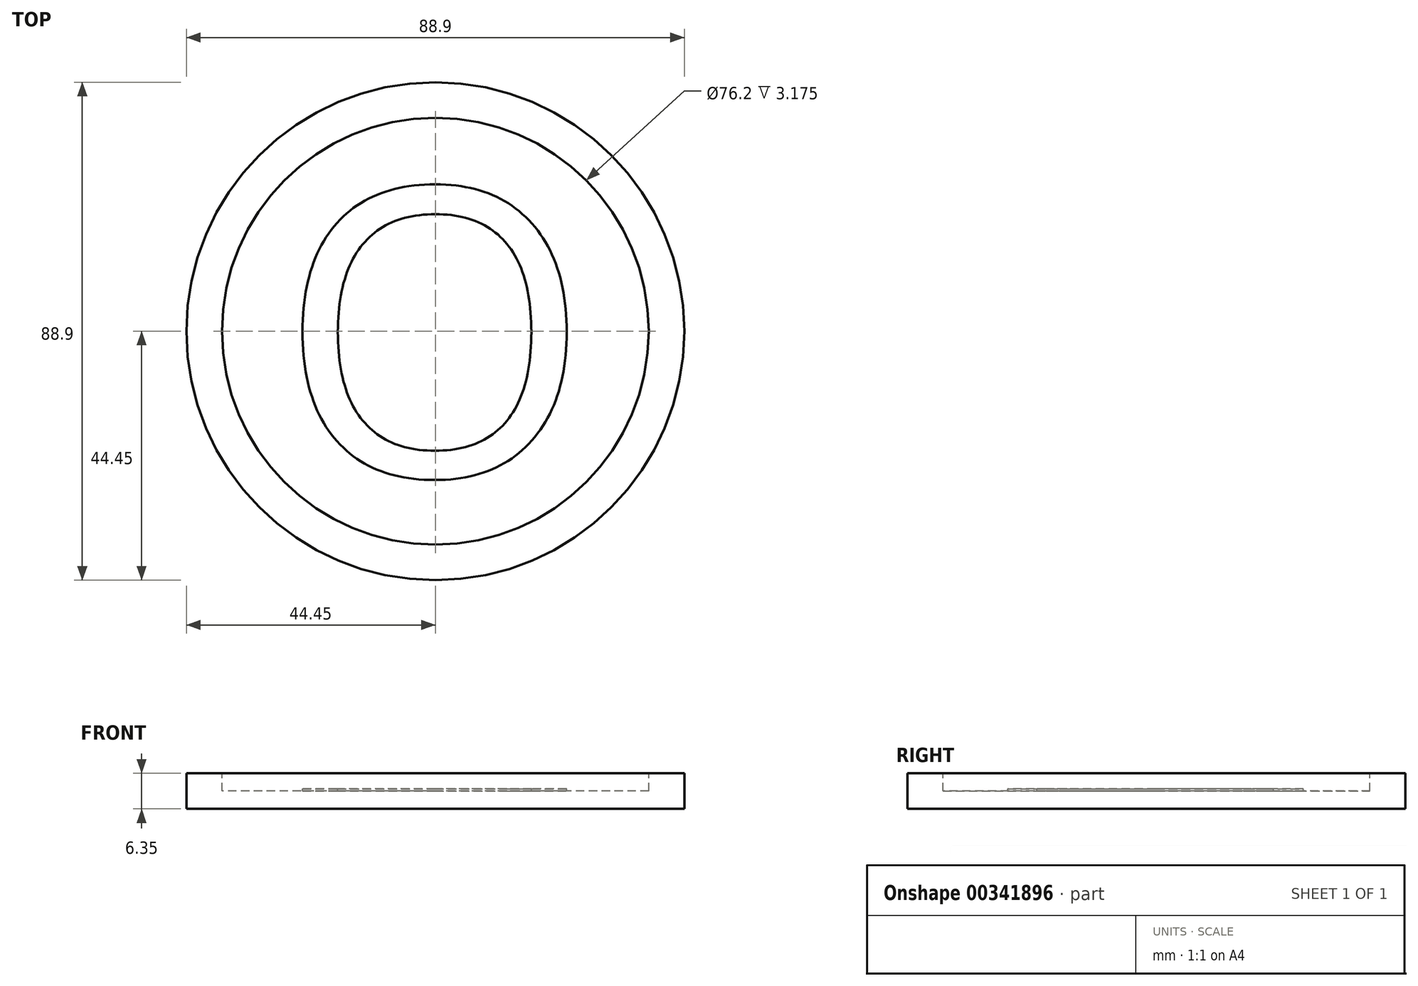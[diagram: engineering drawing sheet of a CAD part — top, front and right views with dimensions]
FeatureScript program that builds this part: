
annotation { "Feature Type Name" : "Feature", "Feature Type Description" : "" }
export const myFeature = defineFeature(function(context is Context, id is Id, definition is map)
    precondition{}
    {
        {
            var Q0;
            Q0=qCreatedBy(makeId("Top.planeOp"),FACE);
            var sketch = newSketch(context, id + "F0", { "sketchPlane" : qUnion([Q0])});
            skCircle(sketch, "E0", {"center": v(0, 0) * mm, "radius": 44.45 * mm});
            skSolve(sketch);
        }
        {
            var Q0;
            Q0=makeQuery(id+"F0.imprint","IMPRINT",FACE,{"disambiguationData":[TD([[makeQuery(id+"F0.imprint","IMPRINT",EDGE,{"derivedFrom":sQuery(id+"F0.wireOp",EDGE,"E0")}),1.0]])]});
            extrude(context, id + "F1", {"entities" : qUnion([Q0]), "depth" : 6.35 * mm});
        }
        {
            var Q0;
            Q0=makeQuery(id+"F1.opExtrude","CAP_FACE",FACE,{"disambiguationData":[OSD([sQuery(id+"F0.wireOp",EDGE,"E0")])],"isStart":false});
            cPlane(context, id + "F2", {"entities" : qUnion([Q0]), "cplaneType" : CPlaneType.OFFSET, "offset" : 0 * mm, "width" : 152.4 * mm, "height" : 152.4 * mm});
        }
        {
            var Q0;
            Q0=qCreatedBy(id+"F2.planeOp",FACE);
            var sketch = newSketch(context, id + "F3", { "sketchPlane" : qUnion([Q0])});
            skCircle(sketch, "E1", {"center": v(0, 0) * mm, "radius": 38.1 * mm});
            skPoint(sketch, "E2", {"position": v(-28.1, -8.08) * mm});
            skPoint(sketch, "E3", {"position": v(-28.1, -25.86) * mm});
            skPoint(sketch, "E4", {"position": v(0, -25.86) * mm});
            skText(sketch, "E5", { "text": "O", "fontName": "OpenSans-Regular.ttf"});
            const initialGuessF3  = {"E5": [-0.0281, -0.02586, 1, 0, 0.05172]};
            skSetInitialGuess(sketch, initialGuessF3);
            skSolve(sketch);
        }
        {
            var Q0;
            Q0=makeQuery(id+"F3.imprint","IMPRINT",FACE,{"disambiguationData":[TD([[makeQuery(id+"F3.imprint","IMPRINT",EDGE,{"derivedFrom":sQuery(id+"F3.wireOp",EDGE,"E1")}),1.0]])]});
            var Q1;
            Q1=makeQuery(id+"F3.imprint","IMPRINT",FACE,{"disambiguationData":[TD([[makeQuery(id+"F3.imprint","IMPRINT",EDGE,{"derivedFrom":sQuery(id+"F3.wireOp",EDGE,"E5.sketch_text.stroke-8")}),1.0]])]});
            extrude(context, id + "F4", {"entities" : qUnion([Q0, Q1]), "operationType" : NewBodyOperationType.REMOVE, "oppositeDirection" : true, "depth" : 3.17 * mm});
        }
        {
            var Q0;
            Q0=makeQuery(id+"F3.imprint","IMPRINT",FACE,{"disambiguationData":[TD([[makeQuery(id+"F3.imprint","IMPRINT",EDGE,{"derivedFrom":sQuery(id+"F3.wireOp",EDGE,"d14bb35a-75a6-4bb5-897b-83483272ae7a.sketch_text.stroke-0")}),-1.0]])]});
            var Q1;
            Q1=makeQuery(id+"F3.imprint","IMPRINT",FACE,{"disambiguationData":[TD([[makeQuery(id+"F3.imprint","IMPRINT",EDGE,{"derivedFrom":sQuery(id+"F3.wireOp",EDGE,"E5.sketch_text.stroke-0")}),-1.0]])]});
            extrude(context, id + "F5", {"entities" : qUnion([Q0, Q1]), "operationType" : NewBodyOperationType.REMOVE, "oppositeDirection" : true, "depth" : 2.8 * mm});
        }
    });
